# Revit family: CENTUM Adapterplatte XL120 Gr 3 quer
name_source: partatom
category: HLS-Bauteile
revit_build: Autodesk Revit 2017 (Build: 20190507_1515(x64)
units: mm (PartAtom-declared; Revit-internal decimal feet)

## family parameters
Basisbauteil = Fläche
Beim Laden mit Abzugskörper schneiden = Nein
Bemaßung runder Anschluss = Durchmesser verwenden
Gemeinsam genutzt = Ja
Raumberechnungspunkt = Nein
Teiletyp = Normal

## types (1)
- CENTUM Adapterplatte XL120 Gr 3 quer
    Artikelnummer = 162120303
    EAN = 4250928458421
    Fabrikat = MEFA
    Firma = MEFA Befestigungs- und Montagesysteme GmbH
    Gewicht = 14.99 kg
    Gewicht pro Bauteil = 14.99 kg
    Höhe Profil = 0 mm  [stored 0 ft]
    Kurztext1 = Adapterplatte CENTUM quer
    Kurztext2 = Größe 3 für XL 120 fsv
    Länge = 0 mm  [stored 0 ft]
    Material = Stahl
    Materialname = S235
    Mengeneinheit = St
    Oberflaeche = feuerstückverzinkt
    Profiltyp = XL 120
    Sicherheitsfaktor = 0
    Stärke = 0 mm  [stored 0 ft]
    Vorgabe-Ansicht = 1219 mm
    vpe = 1 St

note: [stored X ft] marks values corroborated as IEEE doubles in the binary element streams (Revit-internal decimal feet)
